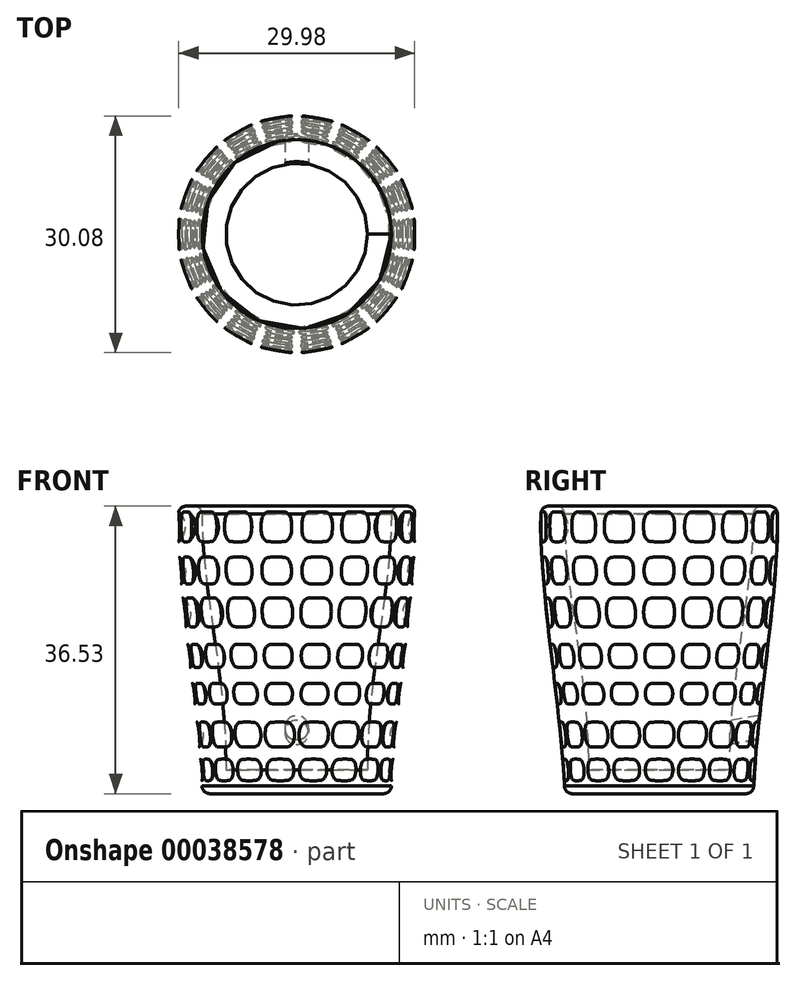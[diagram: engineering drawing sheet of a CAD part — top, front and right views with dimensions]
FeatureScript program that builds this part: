
annotation { "Feature Type Name" : "Feature", "Feature Type Description" : "" }
export const myFeature = defineFeature(function(context is Context, id is Id, definition is map)
    precondition{}
    {
        {
            var Q0;
            Q0=qCreatedBy(makeId("Front.planeOp"),FACE);
            var sketch = newSketch(context, id + "F0", { "sketchPlane" : qUnion([Q0])});
            skFitSpline(sketch, "E0", {"points": [v(-12, 0) * mm, v(-15, 36.53) * mm], "startDerivative": vector(-0.52, 28.45) * mm, "endDerivative": vector(1.31, 30.92) * mm});
            skLineSegment(sketch, "E1", {"start": v(-12, 0) * mm, "end": v(0, 0) * mm});
            skLineSegment(sketch, "E2", {"start": v(-15, 36.53) * mm, "end": v(-12, 36.53) * mm});
            skLineSegment(sketch, "E3", {"start": v(0, 3) * mm, "end": v(0, 0) * mm});
            skFitSpline(sketch, "E4", {"points": [v(-12, 36.53) * mm, v(-9, 3) * mm], "startDerivative": vector(-0.75, -31.04) * mm, "endDerivative": vector(-0.38, -36.79) * mm});
            skLineSegment(sketch, "E5", {"start": v(-9, 3) * mm, "end": v(0, 3) * mm});
            skPoint(sketch, "E6.orphan", {"position": v(0, 36.53) * mm});
            skSolve(sketch);
        }
        {
            var Q0;
            Q0=makeQuery(id+"F0.imprint","IMPRINT",FACE,{"disambiguationData":[TD([[makeQuery(id+"F0.imprint","IMPRINT",EDGE,{"derivedFrom":sQuery(id+"F0.wireOp",EDGE,"E0")}),-1.0]])]});
            var Q1;
            Q1=sQuery(id+"F0.wireOp",EDGE,"E3");
            revolve(context, id + "F1", {"entities" : qUnion([Q0]), "axis" : qUnion([Q1]), "revolveType" : RevolveType.FULL});
        }
        {
            var Q0;
            Q0=qCreatedBy(makeId("Front.planeOp"),FACE);
            var sketch = newSketch(context, id + "F2", { "sketchPlane" : qUnion([Q0])});
            skCircle(sketch, "E7", {"center": v(-16.7, 33.9) * mm, "radius": 2.57 * mm});
            skCircle(sketch, "E8", {"center": v(-16.6, 28.22) * mm, "radius": 2.5 * mm});
            skCircle(sketch, "E9", {"center": v(-15.92, 22.86) * mm, "radius": 2.48 * mm});
            skCircle(sketch, "E10", {"center": v(-15.48, 17.29) * mm, "radius": 2.34 * mm});
            skCircle(sketch, "E11", {"center": v(-14.92, 12.5) * mm, "radius": 2.26 * mm});
            skCircle(sketch, "E12", {"center": v(-14.03, 7.36) * mm, "radius": 2.2 * mm});
            skCircle(sketch, "E13", {"center": v(-13.92, 2.9) * mm, "radius": 2.24 * mm});
            skSolve(sketch);
        }
        {
            var Q0;
            Q0=makeQuery(id+"F2.imprint","IMPRINT",FACE,{"disambiguationData":[TD([[makeQuery(id+"F2.imprint","IMPRINT",EDGE,{"derivedFrom":sQuery(id+"F2.wireOp",EDGE,"E7")}),1.0]])]});
            var Q1;
            Q1=makeQuery(id+"F2.imprint","IMPRINT",FACE,{"disambiguationData":[TD([[makeQuery(id+"F2.imprint","IMPRINT",EDGE,{"derivedFrom":sQuery(id+"F2.wireOp",EDGE,"E8")}),1.0]])]});
            var Q2;
            Q2=makeQuery(id+"F2.imprint","IMPRINT",FACE,{"disambiguationData":[TD([[makeQuery(id+"F2.imprint","IMPRINT",EDGE,{"derivedFrom":sQuery(id+"F2.wireOp",EDGE,"E9")}),1.0]])]});
            var Q3;
            Q3=makeQuery(id+"F2.imprint","IMPRINT",FACE,{"disambiguationData":[TD([[makeQuery(id+"F2.imprint","IMPRINT",EDGE,{"derivedFrom":sQuery(id+"F2.wireOp",EDGE,"E10")}),1.0]])]});
            var Q4;
            Q4=makeQuery(id+"F2.imprint","IMPRINT",FACE,{"disambiguationData":[TD([[makeQuery(id+"F2.imprint","IMPRINT",EDGE,{"derivedFrom":sQuery(id+"F2.wireOp",EDGE,"E11")}),1.0]])]});
            var Q5;
            Q5=makeQuery(id+"F2.imprint","IMPRINT",FACE,{"disambiguationData":[TD([[makeQuery(id+"F2.imprint","IMPRINT",EDGE,{"derivedFrom":sQuery(id+"F2.wireOp",EDGE,"E12")}),1.0]])]});
            var Q6;
            Q6=makeQuery(id+"F2.imprint","IMPRINT",FACE,{"disambiguationData":[TD([[makeQuery(id+"F2.imprint","IMPRINT",EDGE,{"derivedFrom":sQuery(id+"F2.wireOp",EDGE,"E13")}),1.0]])]});
            extrude(context, id + "F3", {"entities" : qUnion([Q0, Q1, Q2, Q3, Q4, Q5, Q6]), "endBound" : BoundingType.SYMMETRIC, "depth" : 4 * mm});
        }
        {
            var Q0;
            Q0=makeQuery(id+"F3.opExtrude","CAP_EDGE",EDGE,{"disambiguationData":[OSD([sQuery(id+"F2.wireOp",EDGE,"E13")])],"isStart":false});
            var Q1;
            Q1=makeQuery(id+"F3.opExtrude","CAP_EDGE",EDGE,{"disambiguationData":[OSD([sQuery(id+"F2.wireOp",EDGE,"E12")])],"isStart":false});
            var Q2;
            Q2=makeQuery(id+"F3.opExtrude","CAP_EDGE",EDGE,{"disambiguationData":[OSD([sQuery(id+"F2.wireOp",EDGE,"E11")])],"isStart":false});
            var Q3;
            Q3=makeQuery(id+"F3.opExtrude","CAP_EDGE",EDGE,{"disambiguationData":[OSD([sQuery(id+"F2.wireOp",EDGE,"E10")])],"isStart":false});
            var Q4;
            Q4=makeQuery(id+"F3.opExtrude","CAP_EDGE",EDGE,{"disambiguationData":[OSD([sQuery(id+"F2.wireOp",EDGE,"E9")])],"isStart":false});
            var Q5;
            Q5=makeQuery(id+"F3.opExtrude","CAP_EDGE",EDGE,{"disambiguationData":[OSD([sQuery(id+"F2.wireOp",EDGE,"E8")])],"isStart":false});
            var Q6;
            Q6=makeQuery(id+"F3.opExtrude","CAP_EDGE",EDGE,{"disambiguationData":[OSD([sQuery(id+"F2.wireOp",EDGE,"E7")])],"isStart":false});
            var Q7;
            Q7=makeQuery(id+"F3.opExtrude","CAP_EDGE",EDGE,{"disambiguationData":[OSD([sQuery(id+"F2.wireOp",EDGE,"E12")])],"isStart":true});
            var Q8;
            Q8=makeQuery(id+"F3.opExtrude","CAP_FACE",FACE,{"disambiguationData":[OSD([sQuery(id+"F2.wireOp",EDGE,"E13")])],"isStart":true});
            var Q9;
            Q9=makeQuery(id+"F3.opExtrude","CAP_EDGE",EDGE,{"disambiguationData":[OSD([sQuery(id+"F2.wireOp",EDGE,"E11")])],"isStart":true});
            var Q10;
            Q10=makeQuery(id+"F3.opExtrude","CAP_EDGE",EDGE,{"disambiguationData":[OSD([sQuery(id+"F2.wireOp",EDGE,"E10")])],"isStart":true});
            var Q11;
            Q11=makeQuery(id+"F3.opExtrude","CAP_EDGE",EDGE,{"disambiguationData":[OSD([sQuery(id+"F2.wireOp",EDGE,"E9")])],"isStart":true});
            var Q12;
            Q12=makeQuery(id+"F3.opExtrude","CAP_EDGE",EDGE,{"disambiguationData":[OSD([sQuery(id+"F2.wireOp",EDGE,"E8")])],"isStart":true});
            var Q13;
            Q13=makeQuery(id+"F3.opExtrude","CAP_EDGE",EDGE,{"disambiguationData":[OSD([sQuery(id+"F2.wireOp",EDGE,"E7")])],"isStart":true});
            fillet(context, id + "F4", {"entities" : qUnion([Q0, Q1, Q2, Q3, Q4, Q5, Q6, Q7, Q8, Q9, Q10, Q11, Q12, Q13]), "radius" : 1 * mm, "tangentPropagation" : true, "allowEdgeOverflow" : false});
        }
        {
            var Q0;
            Q0=makeQuery(id+"F3.opExtrude","SWEPT_BODY",BODY,{"disambiguationData":[OSD([sQuery(id+"F2.wireOp",EDGE,"E7")])]});
            var Q1;
            Q1=makeQuery(id+"F3.opExtrude","SWEPT_BODY",BODY,{"disambiguationData":[OSD([sQuery(id+"F2.wireOp",EDGE,"E8")])]});
            var Q2;
            Q2=makeQuery(id+"F3.opExtrude","SWEPT_BODY",BODY,{"disambiguationData":[OSD([sQuery(id+"F2.wireOp",EDGE,"E9")])]});
            var Q3;
            Q3=makeQuery(id+"F3.opExtrude","SWEPT_BODY",BODY,{"disambiguationData":[OSD([sQuery(id+"F2.wireOp",EDGE,"E10")])]});
            var Q4;
            Q4=makeQuery(id+"F3.opExtrude","SWEPT_BODY",BODY,{"disambiguationData":[OSD([sQuery(id+"F2.wireOp",EDGE,"E11")])]});
            var Q5;
            Q5=makeQuery(id+"F3.opExtrude","SWEPT_BODY",BODY,{"disambiguationData":[OSD([sQuery(id+"F2.wireOp",EDGE,"E12")])]});
            var Q6;
            Q6=makeQuery(id+"F3.opExtrude","SWEPT_BODY",BODY,{"disambiguationData":[OSD([sQuery(id+"F2.wireOp",EDGE,"E13")])]});
            var Q7;
            Q7=sQuery(id+"F0.wireOp",EDGE,"E3");
            circularPattern(context, id + "F5", {"operationType" : NewBodyOperationType.REMOVE, "entities" : qUnion([Q0, Q1, Q2, Q3, Q4, Q5, Q6]), "axis" : qUnion([Q7]), "angle" : 20 * degree, "instanceCount" : 18});
        }
        {
            var Q0;
            Q0=sQuery(id+"F0.wireOp",EDGE,"E1");
            cPlane(context, id + "F6", {"entities" : qUnion([Q0]), "cplaneType" : CPlaneType.LINE_ANGLE, "offset" : 150 * mm, "angle" : 10 * degree, "width" : 150 * mm, "height" : 150 * mm});
        }
        {
            var Q0;
            Q0=qCreatedBy(id+"F6.planeOp",FACE);
            var sketch = newSketch(context, id + "F7", { "sketchPlane" : qUnion([Q0])});
            skCircle(sketch, "E14", {"center": v(0, 6.08) * mm, "radius": 1.5 * mm});
            skSolve(sketch);
        }
        {
            var Q0;
            Q0 = qSketchRegion(id + "F7", true);
            extrude(context, id + "F8", {"entities" : qUnion([Q0]), "operationType" : NewBodyOperationType.REMOVE, "endBound" : BoundingType.THROUGH_ALL, "depth" : 25 * mm});
        }
        {
            var Q0;
            Q0=makeQuery(id+"F1.opRevolve","SWEPT_EDGE",EDGE,{"disambiguationData":[OSD([sQuery(id+"F0.wireOp",EDGE,"E2"),sQuery(id+"F0.wireOp",EDGE,"E4")])]});
            var Q1;
            Q1=makeQuery(id+"F1.opRevolve","SWEPT_EDGE",EDGE,{"disambiguationData":[OSD([sQuery(id+"F0.wireOp",EDGE,"E0"),sQuery(id+"F0.wireOp",EDGE,"E2")])]});
            var Q2;
            Q2=makeQuery(id+"F1.opRevolve","SWEPT_EDGE",EDGE,{"disambiguationData":[OSD([sQuery(id+"F0.wireOp",EDGE,"E0"),sQuery(id+"F0.wireOp",EDGE,"E1")])]});
            fillet(context, id + "F9", {"entities" : qUnion([Q0, Q1, Q2]), "radius" : 1 * mm, "tangentPropagation" : true, "allowEdgeOverflow" : false});
        }
    });
